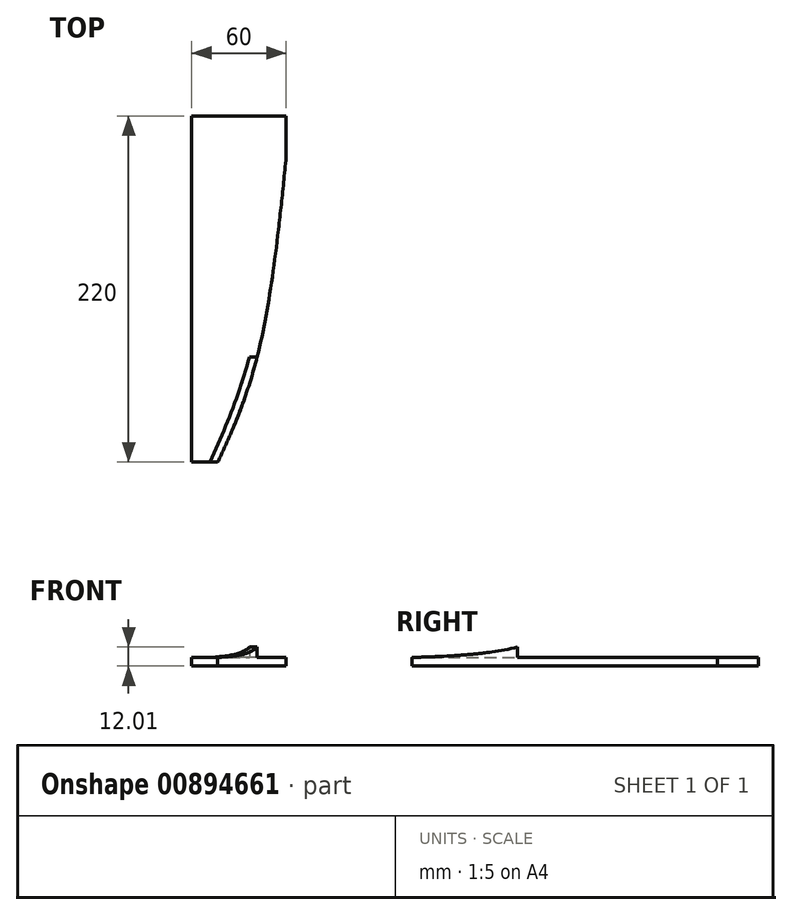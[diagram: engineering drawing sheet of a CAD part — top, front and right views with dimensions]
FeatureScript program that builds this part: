
annotation { "Feature Type Name" : "Feature", "Feature Type Description" : "" }
export const myFeature = defineFeature(function(context is Context, id is Id, definition is map)
    precondition{}
    {
        {
            var Q0;
            Q0=qCreatedBy(makeId("Top.planeOp"),FACE);
            var sketch = newSketch(context, id + "F0", { "sketchPlane" : qUnion([Q0])});
            skLineSegment(sketch, "E0.bottom", {"start": v(30, -110) * mm, "end": v(-30, -110) * mm});
            skLineSegment(sketch, "E0.top", {"start": v(30, 110) * mm, "end": v(-30, 110) * mm});
            skLineSegment(sketch, "E0.left", {"start": v(30, -110) * mm, "end": v(30, 110) * mm});
            skLineSegment(sketch, "E0.right", {"start": v(-30, -110) * mm, "end": v(-30, 110) * mm});
            skPoint(sketch, "E0.middle", {"position": v(0, 0) * mm});
            skSolve(sketch);
        }
        {
            var Q0;
            Q0=makeQuery(id+"F0.imprint","IMPRINT",FACE,{"disambiguationData":[TD([[makeQuery(id+"F0.imprint","IMPRINT",EDGE,{"derivedFrom":sQuery(id+"F0.wireOp",EDGE,"E0.bottom")}),-1.0]])]});
            extrude(context, id + "F1", {"entities" : qUnion([Q0]), "depth" : 60 * mm, "offsetDistance" : 25 * mm});
        }
        {
            var Q0;
            Q0=makeQuery(id+"F1.opExtrude","SWEPT_FACE",FACE,{"disambiguationData":[OSD([sQuery(id+"F0.wireOp",EDGE,"E0.left")])]});
            var sketch = newSketch(context, id + "F2", { "sketchPlane" : qUnion([Q0])});
            skFitSpline(sketch, "E1", {"points": [v(-110, 5.46) * mm, v(-25.11, 18.53) * mm, v(0, 45.37) * mm, v(83.83, 60) * mm], "startDerivative": vector(172.25, 6) * mm, "endDerivative": vector(391.09, 14.4) * mm});
            skSolve(sketch);
        }
        {
            var Q0;
            {var subQ0=sQuery(id+"F2.wireOp",EDGE,"E1");Q0=makeQuery(id+"F2.imprint","IMPRINT",FACE,{"disambiguationData":[TD([[makeQuery(id+"F2.imprint","IMPRINT",EDGE,{"derivedFrom":subQ0}),1.0]])]});}
            extrude(context, id + "F3", {"entities" : qUnion([Q0]), "operationType" : NewBodyOperationType.REMOVE, "endBound" : BoundingType.THROUGH_ALL, "oppositeDirection" : true, "depth" : 25 * mm, "offsetDistance" : 25 * mm});
        }
        {
            var Q0;
            Q0=makeQuery(id+"F1.opExtrude","CAP_FACE",FACE,{"disambiguationData":[OSD([sQuery(id+"F0.wireOp",EDGE,"E0.bottom"),sQuery(id+"F0.wireOp",EDGE,"E0.top"),sQuery(id+"F0.wireOp",EDGE,"E0.left"),sQuery(id+"F0.wireOp",EDGE,"E0.right")])],"isStart":true});
            var sketch = newSketch(context, id + "F4", { "sketchPlane" : qUnion([Q0])});
            skLineSegment(sketch, "E2", {"start": v(30, -110) * mm, "end": v(30, -83.83) * mm});
            skLineSegment(sketch, "E3", {"start": v(30, -83.83) * mm, "end": v(-30, -83.83) * mm});
            skFitSpline(sketch, "E4", {"points": [v(-13.45, 110) * mm, v(11.58, 43.04) * mm, v(30, -83.83) * mm], "startDerivative": vector(66.93, -142.4) * mm, "endDerivative": vector(24.03, -240.56) * mm});
            skLineSegment(sketch, "E5", {"start": v(-13.45, 110) * mm, "end": v(30, 110) * mm});
            skLineSegment(sketch, "E6", {"start": v(-13.45, 110) * mm, "end": v(-18.45, 110) * mm});
            skLineSegment(sketch, "E7", {"start": v(-3.91, 89.7) * mm, "end": v(-8.91, 89.7) * mm});
            skLineSegment(sketch, "E8", {"start": v(11.58, 43.04) * mm, "end": v(6.58, 43.04) * mm});
            skLineSegment(sketch, "E9", {"start": v(25.41, -37.92) * mm, "end": v(20.41, -37.92) * mm});
            skLineSegment(sketch, "E10", {"start": v(30, -83.83) * mm, "end": v(25, -83.83) * mm});
            skFitSpline(sketch, "E11", {"points": [v(-18.45, 110) * mm, v(6.58, 43.04) * mm, v(25, -83.83) * mm], "startDerivative": vector(64.2, -142.74) * mm, "endDerivative": vector(24.62, -240.21) * mm});
            skLineSegment(sketch, "E12", {"start": v(25, -83.83) * mm, "end": v(25, -110) * mm});
            skSolve(sketch);
        }
        {
            var Q0;
            {var subQ6=sQuery(id+"F4.wireOp",EDGE,"E5");Q0=makeQuery(id+"F4.imprint","IMPRINT",FACE,{"disambiguationData":[TD([[makeQuery(id+"F4.imprint","IMPRINT",EDGE,{"derivedFrom":subQ6}),1.0]])]});}
            extrude(context, id + "F5", {"entities" : qUnion([Q0]), "operationType" : NewBodyOperationType.REMOVE, "endBound" : BoundingType.THROUGH_ALL, "oppositeDirection" : true, "depth" : 25 * mm, "offsetDistance" : 25 * mm});
        }
        {
            var Q0;
            {var subQ6=sQuery(id+"F4.wireOp",EDGE,"E3");Q0=makeQuery(id+"F4.imprint","IMPRINT",FACE,{"disambiguationData":[TD([[makeQuery(id+"F4.imprint","IMPRINT",EDGE,{"derivedFrom":subQ6}),-1.0]])]});}
            var Q1;
            {var subQ0=sQuery(id+"F4.wireOp",EDGE,"E3");Q1=makeQuery(id+"F4.imprint","IMPRINT",FACE,{"disambiguationData":[TD([[makeQuery(id+"F4.imprint","IMPRINT",EDGE,{"derivedFrom":subQ0}),1.0]])]});}
            extrude(context, id + "F6", {"entities" : qUnion([Q0, Q1]), "operationType" : NewBodyOperationType.REMOVE, "oppositeDirection" : true, "depth" : 80 * mm, "offsetDistance" : 25 * mm, "hasSecondDirection" : true, "secondDirectionOppositeDirection" : true, "secondDirectionDepth" : 5.46 * mm});
        }
    });
